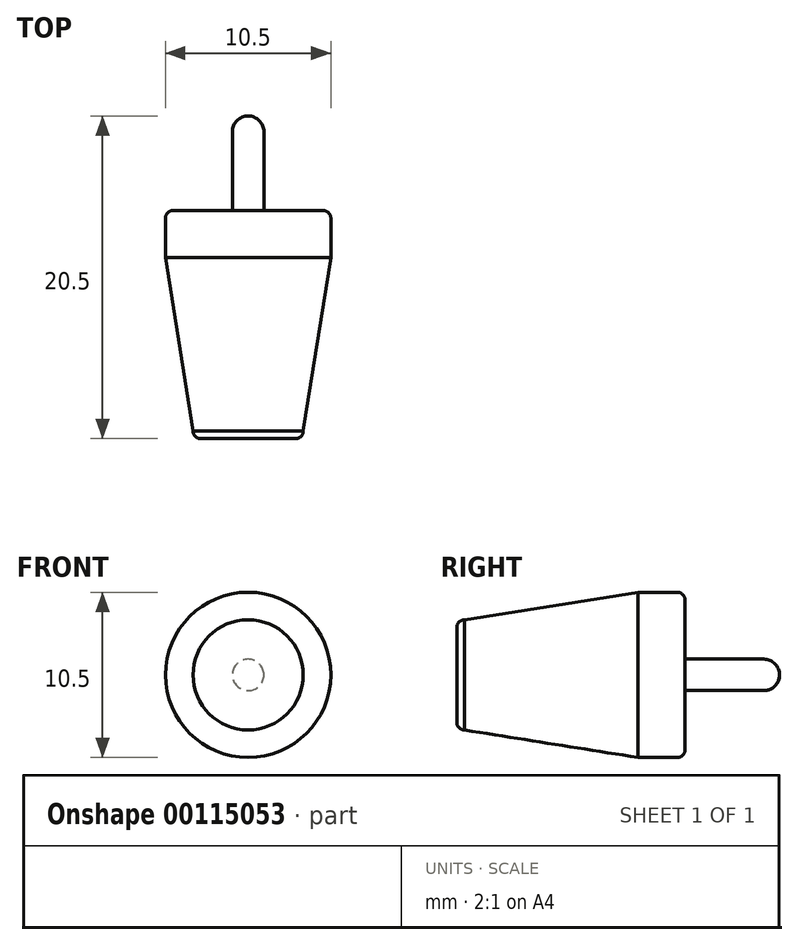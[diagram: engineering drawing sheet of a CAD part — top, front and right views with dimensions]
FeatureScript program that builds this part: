
annotation { "Feature Type Name" : "Feature", "Feature Type Description" : "" }
export const myFeature = defineFeature(function(context is Context, id is Id, definition is map)
    precondition{}
    {
        {
            var Q0;
            Q0=qCreatedBy(makeId("Front.planeOp"),FACE);
            var sketch = newSketch(context, id + "F0", { "sketchPlane" : qUnion([Q0])});
            skCircle(sketch, "E0", {"center": v(0, 0) * mm, "radius": 5.25 * mm});
            skSolve(sketch);
        }
        {
            var Q0;
            Q0=qCreatedBy(makeId("Front.planeOp"),FACE);
            cPlane(context, id + "F1", {"entities" : qUnion([Q0]), "cplaneType" : CPlaneType.OFFSET, "offset" : 14 * mm, "width" : 150 * mm, "height" : 150 * mm});
        }
        {
            var Q0;
            Q0=qCreatedBy(id+"F1.planeOp",FACE);
            var sketch = newSketch(context, id + "F2", { "sketchPlane" : qUnion([Q0])});
            skCircle(sketch, "E1", {"center": v(0, 0) * mm, "radius": 3.5 * mm});
            skSolve(sketch);
        }
        {
            var Q0;
            Q0=makeQuery(id+"F2.imprint","IMPRINT",FACE,{"disambiguationData":[TD([[makeQuery(id+"F2.imprint","IMPRINT",EDGE,{"derivedFrom":sQuery(id+"F2.wireOp",EDGE,"E1")}),1.0]])]});
            extrude(context, id + "F3", {"entities" : qUnion([Q0]), "depth" : .5 * mm});
        }
        {
            var Q0;
            Q0=makeQuery(id+"F0.imprint","IMPRINT",FACE,{"disambiguationData":[TD([[makeQuery(id+"F0.imprint","IMPRINT",EDGE,{"derivedFrom":sQuery(id+"F0.wireOp",EDGE,"E0")}),1.0]])]});
            var Q1;
            Q1=sQuery(id+"F0.wireOp",EDGE,"E0");
            extrude(context, id + "F4", {"entities" : qUnion([Q0]), "surfaceEntities" : qUnion([Q1]), "depth" : 3 * mm});
        }
        {
            var Q0;
            Q0=qCreatedBy(makeId("Front.planeOp"),FACE);
            var sketch = newSketch(context, id + "F5", { "sketchPlane" : qUnion([Q0])});
            skCircle(sketch, "E2", {"center": v(0, 0) * mm, "radius": 1 * mm});
            skSolve(sketch);
        }
        {
            var Q0;
            Q0 = qSketchRegion(id + "F5", true);
            extrude(context, id + "F6", {"entities" : qUnion([Q0]), "operationType" : NewBodyOperationType.ADD, "oppositeDirection" : true, "depth" : 6 * mm});
        }
        {
            var Q0;
            Q0=makeQuery(id+"F3.opExtrude","CAP_FACE",FACE,{"disambiguationData":[OSD([sQuery(id+"F2.wireOp",EDGE,"E1")])],"isStart":true});
            var Q1;
            Q1=makeQuery(id+"F4.opExtrude","CAP_FACE",FACE,{"disambiguationData":[OSD([sQuery(id+"F0.wireOp",EDGE,"E0")])],"isStart":false});
            loft(context, id + "F7", {"sheetProfilesArray" : [{ "sheetProfileEntities" : qUnion([Q0]) }, { "sheetProfileEntities" : qUnion([Q1]) }]});
        }
        {
            var Q0;
            Q0=makeQuery(id+"F3.opExtrude","CAP_EDGE",EDGE,{"disambiguationData":[OSD([sQuery(id+"F2.wireOp",EDGE,"E1")])],"isStart":false});
            fillet(context, id + "F8", {"entities" : qUnion([Q0]), "radius" : .5 * mm, "tangentPropagation" : true, "allowEdgeOverflow" : false});
        }
        {
            var Q0;
            Q0=makeQuery(id+"F4.opExtrude","CAP_EDGE",EDGE,{"disambiguationData":[OSD([sQuery(id+"F0.wireOp",EDGE,"E0")])],"isStart":true});
            fillet(context, id + "F9", {"entities" : qUnion([Q0]), "radius" : .5 * mm, "tangentPropagation" : true, "allowEdgeOverflow" : false});
        }
        {
            var Q0;
            Q0=makeQuery(id+"F6.opExtrude","CAP_EDGE",EDGE,{"disambiguationData":[OSD([sQuery(id+"F5.wireOp",EDGE,"E2")])],"isStart":false});
            fillet(context, id + "F10", {"entities" : qUnion([Q0]), "radius" : 1 * mm, "tangentPropagation" : true, "allowEdgeOverflow" : false});
        }
    });
